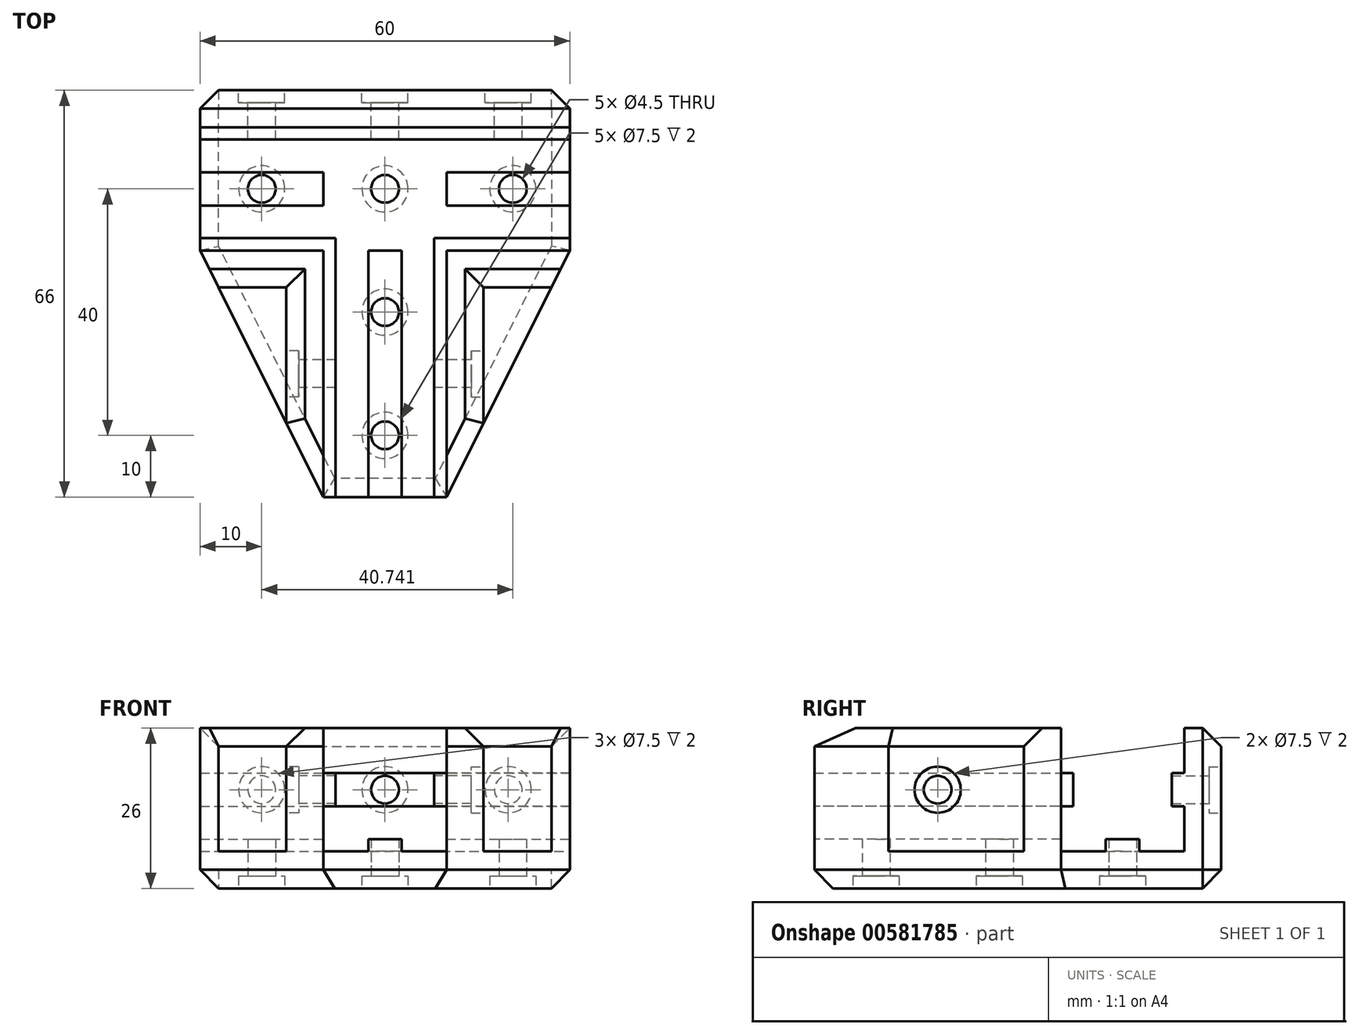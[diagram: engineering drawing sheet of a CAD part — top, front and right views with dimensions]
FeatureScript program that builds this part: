
annotation { "Feature Type Name" : "Feature", "Feature Type Description" : "" }
export const myFeature = defineFeature(function(context is Context, id is Id, definition is map)
    precondition{}
    {
        {
            var Q0;
            Q0=qCreatedBy(makeId("Top.planeOp"),FACE);
            var sketch = newSketch(context, id + "F0", { "sketchPlane" : qUnion([Q0])});
            skLineSegment(sketch, "E0", {"start": v(0, 0) * mm, "end": v(0, 20) * mm, "construction": true});
            skLineSegment(sketch, "E1", {"start": v(0, 0) * mm, "end": v(0, -40) * mm, "construction": true});
            skLineSegment(sketch, "E2", {"start": v(-10, 0) * mm, "end": v(-30, 0) * mm});
            skLineSegment(sketch, "E3", {"start": v(0, 20) * mm, "end": v(-30, 20) * mm});
            skLineSegment(sketch, "E4", {"start": v(-30, 20) * mm, "end": v(-30, 0) * mm});
            skLineSegment(sketch, "E5", {"start": v(0, 20) * mm, "end": v(30, 20) * mm});
            skLineSegment(sketch, "E6", {"start": v(30, 20) * mm, "end": v(30, 0) * mm});
            skLineSegment(sketch, "E7", {"start": v(30, 0) * mm, "end": v(10, 0) * mm});
            skLineSegment(sketch, "E8", {"start": v(0, -40) * mm, "end": v(10, -40) * mm});
            skLineSegment(sketch, "E9", {"start": v(10, -40) * mm, "end": v(10, 0) * mm});
            skLineSegment(sketch, "E10", {"start": v(0, -40) * mm, "end": v(-10, -40) * mm});
            skLineSegment(sketch, "E11", {"start": v(-10, -40) * mm, "end": v(-10, 0) * mm});
            skSolve(sketch);
        }
        {
            var Q0;
            Q0=qSketchRegion(id+"F0",true);
            extrude(context, id + "F1", {"entities" : qUnion([Q0]), "depth" : 6 * mm});
        }
        {
            var Q0;
            Q0=makeQuery(id+"F1.opExtrude","CAP_FACE",FACE,{"disambiguationData":[OSD([sQuery(id+"F0.wireOp",EDGE,"E2"),sQuery(id+"F0.wireOp",EDGE,"E3"),sQuery(id+"F0.wireOp",EDGE,"E4"),sQuery(id+"F0.wireOp",EDGE,"E5"),sQuery(id+"F0.wireOp",EDGE,"E6"),sQuery(id+"F0.wireOp",EDGE,"E7"),sQuery(id+"F0.wireOp",EDGE,"E8"),sQuery(id+"F0.wireOp",EDGE,"E9"),sQuery(id+"F0.wireOp",EDGE,"E10"),sQuery(id+"F0.wireOp",EDGE,"E11")])],"isStart":false});
            var sketch = newSketch(context, id + "F2", { "sketchPlane" : qUnion([Q0])});
            skLineSegment(sketch, "E12", {"start": v(-30, 10) * mm, "end": v(30, 10) * mm, "construction": true});
            skLineSegment(sketch, "E13", {"start": v(0, -40) * mm, "end": v(0, 0) * mm, "construction": true});
            skLineSegment(sketch, "E14", {"start": v(0, 0) * mm, "end": v(-2.71, 0) * mm});
            skLineSegment(sketch, "E15", {"start": v(-2.71, 0) * mm, "end": v(-2.7, -40) * mm});
            skLineSegment(sketch, "E16", {"start": v(2.71, -40) * mm, "end": v(2.71, 0) * mm});
            skLineSegment(sketch, "E17", {"start": v(2.71, 0) * mm, "end": v(0, 0) * mm});
            skLineSegment(sketch, "E18", {"start": v(-2.7, -40) * mm, "end": v(2.71, -40) * mm});
            skLineSegment(sketch, "E19", {"start": v(10, 10) * mm, "end": v(10, 12.7) * mm});
            skLineSegment(sketch, "E20", {"start": v(10, 12.71) * mm, "end": v(30, 12.71) * mm});
            skLineSegment(sketch, "E21", {"start": v(30, 12.71) * mm, "end": v(30, 7.3) * mm});
            skLineSegment(sketch, "E22", {"start": v(30, 7.3) * mm, "end": v(10, 7.29) * mm});
            skLineSegment(sketch, "E23", {"start": v(10, 7.29) * mm, "end": v(10, 10) * mm});
            skLineSegment(sketch, "E24", {"start": v(-30, 12.71) * mm, "end": v(-30, 7.29) * mm});
            skLineSegment(sketch, "E25", {"start": v(-30, 7.29) * mm, "end": v(-10, 7.3) * mm});
            skLineSegment(sketch, "E26", {"start": v(-10, 7.29) * mm, "end": v(-10, 12.71) * mm});
            skLineSegment(sketch, "E27", {"start": v(-10, 12.71) * mm, "end": v(-30, 12.71) * mm});
            skSolve(sketch);
        }
        {
            var Q0;
            Q0=qSketchRegion(id+"F2",true);
            extrude(context, id + "F3", {"entities" : qUnion([Q0]), "operationType" : NewBodyOperationType.ADD, "depth" : 2 * mm});
        }
        {
            var Q0;
            Q0=makeQuery(id+"F1.opExtrude","CAP_FACE",FACE,{"disambiguationData":[OSD([sQuery(id+"F0.wireOp",EDGE,"E2"),sQuery(id+"F0.wireOp",EDGE,"E3"),sQuery(id+"F0.wireOp",EDGE,"E4"),sQuery(id+"F0.wireOp",EDGE,"E5"),sQuery(id+"F0.wireOp",EDGE,"E6"),sQuery(id+"F0.wireOp",EDGE,"E7"),sQuery(id+"F0.wireOp",EDGE,"E8"),sQuery(id+"F0.wireOp",EDGE,"E9"),sQuery(id+"F0.wireOp",EDGE,"E10"),sQuery(id+"F0.wireOp",EDGE,"E11")])],"isStart":true});
            var sketch = newSketch(context, id + "F4", { "sketchPlane" : qUnion([Q0])});
            skCircle(sketch, "E28", {"center": v(-20, -10) * mm, "radius": 2.25 * mm});
            skCircle(sketch, "E29", {"center": v(0, 10) * mm, "radius": 2.25 * mm});
            skCircle(sketch, "E30", {"center": v(0, 30) * mm, "radius": 2.25 * mm});
            skCircle(sketch, "E31", {"center": v(20.74, -10) * mm, "radius": 2.25 * mm});
            skCircle(sketch, "E32", {"center": v(0, -10) * mm, "radius": 2.25 * mm});
            skSolve(sketch);
        }
        {
            var Q0;
            Q0=qSketchRegion(id+"F4",true);
            extrude(context, id + "F5", {"entities" : qUnion([Q0]), "operationType" : NewBodyOperationType.REMOVE, "endBound" : BoundingType.THROUGH_ALL, "oppositeDirection" : true, "depth" : 25 * mm});
        }
        {
            var Q0;
            Q0=makeQuery(id+"F1.opExtrude","CAP_FACE",FACE,{"disambiguationData":[OSD([sQuery(id+"F0.wireOp",EDGE,"E2"),sQuery(id+"F0.wireOp",EDGE,"E3"),sQuery(id+"F0.wireOp",EDGE,"E4"),sQuery(id+"F0.wireOp",EDGE,"E5"),sQuery(id+"F0.wireOp",EDGE,"E6"),sQuery(id+"F0.wireOp",EDGE,"E7"),sQuery(id+"F0.wireOp",EDGE,"E8"),sQuery(id+"F0.wireOp",EDGE,"E9"),sQuery(id+"F0.wireOp",EDGE,"E10"),sQuery(id+"F0.wireOp",EDGE,"E11")])],"isStart":true});
            var sketch = newSketch(context, id + "F6", { "sketchPlane" : qUnion([Q0])});
            skCircle(sketch, "E33", {"center": v(0, 30) * mm, "radius": 3.75 * mm});
            skCircle(sketch, "E34", {"center": v(0, 10) * mm, "radius": 3.75 * mm});
            skCircle(sketch, "E35", {"center": v(20.74, -10) * mm, "radius": 3.75 * mm});
            skCircle(sketch, "E36", {"center": v(-20, -10) * mm, "radius": 3.75 * mm});
            skCircle(sketch, "E37", {"center": v(0, -10) * mm, "radius": 3.75 * mm});
            skSolve(sketch);
        }
        {
            var Q0;
            Q0=qSketchRegion(id+"F6",true);
            extrude(context, id + "F7", {"entities" : qUnion([Q0]), "operationType" : NewBodyOperationType.REMOVE, "oppositeDirection" : true, "depth" : 2 * mm});
        }
        {
            var Q0;
            Q0=makeQuery(id+"F1.opExtrude","CAP_FACE",FACE,{"disambiguationData":[OSD([sQuery(id+"F0.wireOp",EDGE,"E2"),sQuery(id+"F0.wireOp",EDGE,"E3"),sQuery(id+"F0.wireOp",EDGE,"E4"),sQuery(id+"F0.wireOp",EDGE,"E5"),sQuery(id+"F0.wireOp",EDGE,"E6"),sQuery(id+"F0.wireOp",EDGE,"E7"),sQuery(id+"F0.wireOp",EDGE,"E8"),sQuery(id+"F0.wireOp",EDGE,"E9"),sQuery(id+"F0.wireOp",EDGE,"E10"),sQuery(id+"F0.wireOp",EDGE,"E11")])],"isStart":true});
            var sketch = newSketch(context, id + "F8", { "sketchPlane" : qUnion([Q0])});
            skLineSegment(sketch, "E38", {"start": v(-10, 40) * mm, "end": v(-30, 0) * mm});
            skLineSegment(sketch, "E39", {"start": v(-30, 0) * mm, "end": v(-10, 0) * mm});
            skLineSegment(sketch, "E40", {"start": v(-10, 0) * mm, "end": v(-10, 40) * mm});
            skLineSegment(sketch, "E41", {"start": v(10, 40) * mm, "end": v(10, 0) * mm});
            skLineSegment(sketch, "E42", {"start": v(10, 0) * mm, "end": v(30, 0) * mm});
            skLineSegment(sketch, "E43", {"start": v(30, 0) * mm, "end": v(10, 40) * mm});
            skLineSegment(sketch, "E44", {"start": v(-30, -20) * mm, "end": v(-30, -26) * mm});
            skLineSegment(sketch, "E45", {"start": v(-30, -26) * mm, "end": v(30, -26) * mm});
            skLineSegment(sketch, "E46", {"start": v(30, -26) * mm, "end": v(30, -20) * mm});
            skLineSegment(sketch, "E47", {"start": v(30, -20) * mm, "end": v(-30, -20) * mm});
            skSolve(sketch);
        }
        {
            var Q0;
            Q0=qSketchRegion(id+"F8",true);
            extrude(context, id + "F9", {"entities" : qUnion([Q0]), "operationType" : NewBodyOperationType.ADD, "oppositeDirection" : true, "depth" : 6 * mm});
        }
        {
            var Q0;
            Q0=makeQuery(id+"F9.boolean.opBoolean","MERGE",FACE,{"derivedFrom":[makeQuery(id+"F1.opExtrude","CAP_FACE",FACE,{"disambiguationData":[OSD([sQuery(id+"F0.wireOp",EDGE,"E2"),sQuery(id+"F0.wireOp",EDGE,"E3"),sQuery(id+"F0.wireOp",EDGE,"E4"),sQuery(id+"F0.wireOp",EDGE,"E5"),sQuery(id+"F0.wireOp",EDGE,"E6"),sQuery(id+"F0.wireOp",EDGE,"E7"),sQuery(id+"F0.wireOp",EDGE,"E8"),sQuery(id+"F0.wireOp",EDGE,"E9"),sQuery(id+"F0.wireOp",EDGE,"E10"),sQuery(id+"F0.wireOp",EDGE,"E11")])],"isStart":false}),makeQuery(id+"F9.opExtrude","CAP_FACE",FACE,{"disambiguationData":[OSD([sQuery(id+"F8.wireOp",EDGE,"E38"),sQuery(id+"F8.wireOp",EDGE,"E39"),sQuery(id+"F8.wireOp",EDGE,"E40")])],"isStart":false}),makeQuery(id+"F9.opExtrude","CAP_FACE",FACE,{"disambiguationData":[OSD([sQuery(id+"F8.wireOp",EDGE,"E41"),sQuery(id+"F8.wireOp",EDGE,"E42"),sQuery(id+"F8.wireOp",EDGE,"E43")])],"isStart":false})]});
            var sketch = newSketch(context, id + "F10", { "sketchPlane" : qUnion([Q0])});
            skLineSegment(sketch, "E48", {"start": v(0, 0) * mm, "end": v(10, 0) * mm, "construction": true});
            skPoint(sketch, "E48.endSnap0", {"position": v(0, 0) * mm});
            skLineSegment(sketch, "E49", {"start": v(0, 0) * mm, "end": v(-10, 0) * mm, "construction": true});
            skLineSegment(sketch, "E50", {"start": v(10, 0) * mm, "end": v(10, -40) * mm});
            skLineSegment(sketch, "E51", {"start": v(10, 0) * mm, "end": v(30, 0) * mm});
            skLineSegment(sketch, "E52", {"start": v(20, 0) * mm, "end": v(20, -6) * mm, "construction": true});
            skLineSegment(sketch, "E53", {"start": v(10, -20) * mm, "end": v(16, -20) * mm, "construction": true});
            skLineSegment(sketch, "E54", {"start": v(27, -6) * mm, "end": v(16, -6) * mm});
            skLineSegment(sketch, "E55", {"start": v(16, -6) * mm, "end": v(16, -28) * mm});
            skLineSegment(sketch, "E56", {"start": v(16, -28) * mm, "end": v(10, -40) * mm});
            skLineSegment(sketch, "E57", {"start": v(27, -6) * mm, "end": v(30, 0) * mm});
            skLineSegment(sketch, "E58", {"start": v(-10, 0) * mm, "end": v(-10, -40) * mm});
            skLineSegment(sketch, "E59", {"start": v(-30, 0) * mm, "end": v(-10, 0) * mm});
            skLineSegment(sketch, "E60", {"start": v(-20, 0) * mm, "end": v(-20, -6) * mm, "construction": true});
            skLineSegment(sketch, "E61", {"start": v(-10, -20) * mm, "end": v(-16, -20) * mm, "construction": true});
            skLineSegment(sketch, "E62", {"start": v(-27, -6) * mm, "end": v(-16, -6) * mm});
            skLineSegment(sketch, "E63", {"start": v(-16, -6) * mm, "end": v(-16, -28) * mm});
            skLineSegment(sketch, "E64", {"start": v(-16, -28) * mm, "end": v(-10, -40) * mm});
            skLineSegment(sketch, "E65", {"start": v(-27, -6) * mm, "end": v(-30, 0) * mm});
            skLineSegment(sketch, "E66.bottom", {"start": v(-30, 26) * mm, "end": v(30, 26) * mm});
            skLineSegment(sketch, "E66.top", {"start": v(-30, 20) * mm, "end": v(30, 20) * mm});
            skLineSegment(sketch, "E66.left", {"start": v(-30, 26) * mm, "end": v(-30, 20) * mm});
            skLineSegment(sketch, "E66.right", {"start": v(30, 26) * mm, "end": v(30, 20) * mm});
            skSolve(sketch);
        }
        {
            var Q0;
            Q0=qSketchRegion(id+"F10",true);
            extrude(context, id + "F11", {"entities" : qUnion([Q0]), "operationType" : NewBodyOperationType.ADD, "depth" : 20 * mm});
        }
        {
            var Q0;
            Q0=makeQuery(id+"F11.boolean.opBoolean","MERGE",FACE,{"derivedFrom":[makeQuery(id+"F9.boolean.opBoolean","MERGE",FACE,{"derivedFrom":[makeQuery(id+"F3.boolean.opBoolean","MERGE",FACE,{"derivedFrom":[makeQuery(id+"F1.opExtrude","SWEPT_FACE",FACE,{"disambiguationData":[OSD([sQuery(id+"F0.wireOp",EDGE,"E6")])]}),makeQuery(id+"F3.opExtrude","SWEPT_FACE",FACE,{"disambiguationData":[OSD([sQuery(id+"F2.wireOp",EDGE,"E21")])]})]}),makeQuery(id+"F9.opExtrude","SWEPT_FACE",FACE,{"disambiguationData":[OSD([sQuery(id+"F8.wireOp",EDGE,"E46")])]})]}),makeQuery(id+"F11.opExtrude","SWEPT_FACE",FACE,{"disambiguationData":[OSD([sQuery(id+"F10.wireOp",EDGE,"E66.right")])]})]});
            var sketch = newSketch(context, id + "F12", { "sketchPlane" : qUnion([Q0])});
            skLineSegment(sketch, "E67", {"start": v(20, 16) * mm, "end": v(20, 13.29) * mm});
            skLineSegment(sketch, "E68", {"start": v(20, 13.29) * mm, "end": v(18, 13.29) * mm});
            skLineSegment(sketch, "E69", {"start": v(18, 13.29) * mm, "end": v(18, 18.71) * mm});
            skLineSegment(sketch, "E70", {"start": v(18, 18.71) * mm, "end": v(20, 18.71) * mm});
            skLineSegment(sketch, "E71", {"start": v(20, 18.71) * mm, "end": v(20, 16) * mm});
            skSolve(sketch);
        }
        {
            var Q0;
            Q0=qSketchRegion(id+"F12",true);
            extrude(context, id + "F13", {"entities" : qUnion([Q0]), "operationType" : NewBodyOperationType.ADD, "oppositeDirection" : true, "depth" : 60 * mm});
        }
        {
            var Q0;
            Q0=makeQuery(id+"F11.opExtrude","SWEPT_FACE",FACE,{"disambiguationData":[OSD([sQuery(id+"F10.wireOp",EDGE,"E58")])]});
            var sketch = newSketch(context, id + "F14", { "sketchPlane" : qUnion([Q0])});
            skLineSegment(sketch, "E72", {"start": v(0, 16) * mm, "end": v(0, 18.71) * mm});
            skLineSegment(sketch, "E73", {"start": v(0, 18.71) * mm, "end": v(2, 18.71) * mm});
            skLineSegment(sketch, "E74", {"start": v(2, 18.71) * mm, "end": v(2, 13.29) * mm});
            skLineSegment(sketch, "E75", {"start": v(2, 13.29) * mm, "end": v(0, 13.29) * mm});
            skLineSegment(sketch, "E76", {"start": v(0, 13.29) * mm, "end": v(0, 16) * mm});
            skSolve(sketch);
        }
        {
            var Q0;
            Q0=qSketchRegion(id+"F14",true);
            extrude(context, id + "F15", {"entities" : qUnion([Q0]), "operationType" : NewBodyOperationType.ADD, "oppositeDirection" : true, "depth" : 20 * mm});
        }
        {
            var Q0;
            Q0=makeQuery(id+"F15.boolean.opBoolean","MERGE",FACE,{"derivedFrom":[makeQuery(id+"F11.opExtrude","SWEPT_FACE",FACE,{"disambiguationData":[OSD([sQuery(id+"F10.wireOp",EDGE,"E58")])]}),makeQuery(id+"F15.opExtrude","CAP_FACE",FACE,{"disambiguationData":[OSD([sQuery(id+"F14.wireOp",EDGE,"E72"),sQuery(id+"F14.wireOp",EDGE,"E73"),sQuery(id+"F14.wireOp",EDGE,"E74"),sQuery(id+"F14.wireOp",EDGE,"E75"),sQuery(id+"F14.wireOp",EDGE,"E76")])],"isStart":true})]});
            var sketch = newSketch(context, id + "F16", { "sketchPlane" : qUnion([Q0])});
            skLineSegment(sketch, "E77.bottom", {"start": v(2, 18.71) * mm, "end": v(-40, 18.71) * mm});
            skLineSegment(sketch, "E77.top", {"start": v(2, 13.29) * mm, "end": v(-40, 13.29) * mm});
            skLineSegment(sketch, "E77.left", {"start": v(2, 18.71) * mm, "end": v(2, 13.29) * mm});
            skLineSegment(sketch, "E77.right", {"start": v(-40, 18.71) * mm, "end": v(-40, 13.29) * mm});
            skSolve(sketch);
        }
        {
            var Q0;
            Q0=qSketchRegion(id+"F16",true);
            extrude(context, id + "F17", {"entities" : qUnion([Q0]), "operationType" : NewBodyOperationType.ADD, "depth" : 2 * mm});
        }
        {
            var Q0;
            Q0=makeQuery(id+"F11.opExtrude","SWEPT_FACE",FACE,{"disambiguationData":[OSD([sQuery(id+"F10.wireOp",EDGE,"E50")])]});
            var sketch = newSketch(context, id + "F18", { "sketchPlane" : qUnion([Q0])});
            skLineSegment(sketch, "E78", {"start": v(0, 16) * mm, "end": v(0, 18.71) * mm});
            skLineSegment(sketch, "E79", {"start": v(0, 18.71) * mm, "end": v(-2, 18.71) * mm});
            skLineSegment(sketch, "E80", {"start": v(-2, 18.71) * mm, "end": v(-2, 13.29) * mm});
            skLineSegment(sketch, "E81", {"start": v(-2, 13.29) * mm, "end": v(0, 13.29) * mm});
            skLineSegment(sketch, "E82", {"start": v(0, 13.29) * mm, "end": v(0, 16) * mm});
            skSolve(sketch);
        }
        {
            var Q0;
            Q0=qSketchRegion(id+"F18",true);
            extrude(context, id + "F19", {"entities" : qUnion([Q0]), "operationType" : NewBodyOperationType.ADD, "oppositeDirection" : true, "depth" : 20 * mm});
        }
        {
            var Q0;
            Q0=makeQuery(id+"F19.boolean.opBoolean","MERGE",FACE,{"derivedFrom":[makeQuery(id+"F11.opExtrude","SWEPT_FACE",FACE,{"disambiguationData":[OSD([sQuery(id+"F10.wireOp",EDGE,"E50")])]}),makeQuery(id+"F19.opExtrude","CAP_FACE",FACE,{"disambiguationData":[OSD([sQuery(id+"F18.wireOp",EDGE,"E78"),sQuery(id+"F18.wireOp",EDGE,"E79"),sQuery(id+"F18.wireOp",EDGE,"E80"),sQuery(id+"F18.wireOp",EDGE,"E81"),sQuery(id+"F18.wireOp",EDGE,"E82")])],"isStart":true})]});
            var sketch = newSketch(context, id + "F20", { "sketchPlane" : qUnion([Q0])});
            skLineSegment(sketch, "E83.bottom", {"start": v(-2, 13.29) * mm, "end": v(40, 13.29) * mm});
            skLineSegment(sketch, "E83.top", {"start": v(-2, 18.71) * mm, "end": v(40, 18.71) * mm});
            skLineSegment(sketch, "E83.left", {"start": v(-2, 13.29) * mm, "end": v(-2, 18.71) * mm});
            skLineSegment(sketch, "E83.right", {"start": v(40, 13.29) * mm, "end": v(40, 18.71) * mm});
            skSolve(sketch);
        }
        {
            var Q0;
            Q0=qSketchRegion(id+"F20",true);
            extrude(context, id + "F21", {"entities" : qUnion([Q0]), "operationType" : NewBodyOperationType.ADD, "depth" : 2 * mm});
        }
        {
            var Q0;
            Q0=makeQuery(id+"F11.opExtrude","SWEPT_FACE",FACE,{"disambiguationData":[OSD([sQuery(id+"F10.wireOp",EDGE,"E63")])]});
            var sketch = newSketch(context, id + "F22", { "sketchPlane" : qUnion([Q0])});
            skCircle(sketch, "E84", {"center": v(20, 16) * mm, "radius": 2.25 * mm});
            skSolve(sketch);
        }
        {
            var Q0;
            Q0=qSketchRegion(id+"F22",true);
            extrude(context, id + "F23", {"entities" : qUnion([Q0]), "operationType" : NewBodyOperationType.REMOVE, "endBound" : BoundingType.THROUGH_ALL, "oppositeDirection" : true, "depth" : 25 * mm});
        }
        {
            var Q0;
            Q0=makeQuery(id+"F11.boolean.opBoolean","MERGE",FACE,{"derivedFrom":[makeQuery(id+"F9.opExtrude","SWEPT_FACE",FACE,{"disambiguationData":[OSD([sQuery(id+"F8.wireOp",EDGE,"E45")])]}),makeQuery(id+"F11.opExtrude","SWEPT_FACE",FACE,{"disambiguationData":[OSD([sQuery(id+"F10.wireOp",EDGE,"E66.bottom")])]})]});
            var sketch = newSketch(context, id + "F24", { "sketchPlane" : qUnion([Q0])});
            skCircle(sketch, "E85", {"center": v(-20, 16) * mm, "radius": 2.25 * mm});
            skCircle(sketch, "E86", {"center": v(0, 16) * mm, "radius": 2.25 * mm});
            skCircle(sketch, "E87", {"center": v(20, 16) * mm, "radius": 2.25 * mm});
            skSolve(sketch);
        }
        {
            var Q0;
            Q0=qSketchRegion(id+"F24",true);
            extrude(context, id + "F25", {"entities" : qUnion([Q0]), "operationType" : NewBodyOperationType.REMOVE, "endBound" : BoundingType.UP_TO_NEXT, "oppositeDirection" : true, "depth" : 8 * mm});
        }
        {
            var Q0;
            Q0=makeQuery(id+"F11.opExtrude","SWEPT_FACE",FACE,{"disambiguationData":[OSD([sQuery(id+"F10.wireOp",EDGE,"E55")])]});
            var sketch = newSketch(context, id + "F26", { "sketchPlane" : qUnion([Q0])});
            skCircle(sketch, "E88", {"center": v(-20, 16) * mm, "radius": 3.75 * mm});
            skSolve(sketch);
        }
        {
            var Q0;
            Q0=qSketchRegion(id+"F26",true);
            extrude(context, id + "F27", {"entities" : qUnion([Q0]), "operationType" : NewBodyOperationType.REMOVE, "oppositeDirection" : true, "depth" : 2 * mm});
        }
        {
            var Q0;
            Q0=makeQuery(id+"F11.opExtrude","SWEPT_FACE",FACE,{"disambiguationData":[OSD([sQuery(id+"F10.wireOp",EDGE,"E63")])]});
            var sketch = newSketch(context, id + "F28", { "sketchPlane" : qUnion([Q0])});
            skCircle(sketch, "E89", {"center": v(20, 16) * mm, "radius": 3.75 * mm});
            skSolve(sketch);
        }
        {
            var Q0;
            Q0=qSketchRegion(id+"F28",true);
            extrude(context, id + "F29", {"entities" : qUnion([Q0]), "operationType" : NewBodyOperationType.REMOVE, "oppositeDirection" : true, "depth" : 2 * mm});
        }
        {
            var Q0;
            Q0=makeQuery(id+"F11.boolean.opBoolean","MERGE",FACE,{"derivedFrom":[makeQuery(id+"F9.opExtrude","SWEPT_FACE",FACE,{"disambiguationData":[OSD([sQuery(id+"F8.wireOp",EDGE,"E45")])]}),makeQuery(id+"F11.opExtrude","SWEPT_FACE",FACE,{"disambiguationData":[OSD([sQuery(id+"F10.wireOp",EDGE,"E66.bottom")])]})]});
            var sketch = newSketch(context, id + "F30", { "sketchPlane" : qUnion([Q0])});
            skCircle(sketch, "E90", {"center": v(-20, 16) * mm, "radius": 3.75 * mm});
            skCircle(sketch, "E91", {"center": v(0, 16) * mm, "radius": 3.75 * mm});
            skCircle(sketch, "E92", {"center": v(20, 16) * mm, "radius": 3.75 * mm});
            skSolve(sketch);
        }
        {
            var Q0;
            Q0=qSketchRegion(id+"F30",true);
            extrude(context, id + "F31", {"entities" : qUnion([Q0]), "operationType" : NewBodyOperationType.REMOVE, "oppositeDirection" : true, "depth" : 2 * mm});
        }
        {
            var Q0;
            Q0=makeQuery(id+"F9.opExtrude","CAP_EDGE",EDGE,{"disambiguationData":[OSD([sQuery(id+"F8.wireOp",EDGE,"E45")])],"isStart":true});
            var Q1;
            Q1=makeQuery(id+"F11.boolean.opBoolean","MERGE",EDGE,{"derivedFrom":[makeQuery(id+"F9.opExtrude","SWEPT_EDGE",EDGE,{"disambiguationData":[OSD([sQuery(id+"F8.wireOp",EDGE,"E45"),sQuery(id+"F8.wireOp",EDGE,"E46")])]}),makeQuery(id+"F11.opExtrude","SWEPT_EDGE",EDGE,{"disambiguationData":[OSD([sQuery(id+"F10.wireOp",EDGE,"E66.bottom"),sQuery(id+"F10.wireOp",EDGE,"E66.right")])]})]});
            var Q2;
            Q2=makeQuery(id+"F11.boolean.opBoolean","MERGE",EDGE,{"derivedFrom":[makeQuery(id+"F9.opExtrude","SWEPT_EDGE",EDGE,{"disambiguationData":[OSD([sQuery(id+"F8.wireOp",EDGE,"E44"),sQuery(id+"F8.wireOp",EDGE,"E45")])]}),makeQuery(id+"F11.opExtrude","SWEPT_EDGE",EDGE,{"disambiguationData":[OSD([sQuery(id+"F10.wireOp",EDGE,"E66.bottom"),sQuery(id+"F10.wireOp",EDGE,"E66.left")])]})]});
            var Q3;
            Q3=makeQuery(id+"F9.boolean.opBoolean","MERGE",EDGE,{"derivedFrom":[makeQuery(id+"F1.opExtrude","CAP_EDGE",EDGE,{"disambiguationData":[OSD([sQuery(id+"F0.wireOp",EDGE,"E4")])],"isStart":true}),makeQuery(id+"F9.opExtrude","CAP_EDGE",EDGE,{"disambiguationData":[OSD([sQuery(id+"F8.wireOp",EDGE,"E44")])],"isStart":true})]});
            var Q4;
            Q4=makeQuery(id+"F9.boolean.opBoolean","MERGE",EDGE,{"derivedFrom":[makeQuery(id+"F1.opExtrude","CAP_EDGE",EDGE,{"disambiguationData":[OSD([sQuery(id+"F0.wireOp",EDGE,"E6")])],"isStart":true}),makeQuery(id+"F9.opExtrude","CAP_EDGE",EDGE,{"disambiguationData":[OSD([sQuery(id+"F8.wireOp",EDGE,"E46")])],"isStart":true})]});
            var Q5;
            Q5=makeQuery(id+"F9.opExtrude","CAP_EDGE",EDGE,{"disambiguationData":[OSD([sQuery(id+"F8.wireOp",EDGE,"E43")])],"isStart":true});
            var Q6;
            Q6=makeQuery(id+"F9.opExtrude","CAP_EDGE",EDGE,{"disambiguationData":[OSD([sQuery(id+"F8.wireOp",EDGE,"E38")])],"isStart":true});
            var Q7;
            Q7=makeQuery(id+"F1.opExtrude","CAP_EDGE",EDGE,{"disambiguationData":[OSD([sQuery(id+"F0.wireOp",EDGE,"E8"),sQuery(id+"F0.wireOp",EDGE,"E10")])],"isStart":true});
            var Q8;
            Q8=makeQuery(id+"F11.opExtrude","CAP_EDGE",EDGE,{"disambiguationData":[OSD([sQuery(id+"F10.wireOp",EDGE,"E66.bottom")])],"isStart":false});
            var Q9;
            Q9=makeQuery(id+"F11.opExtrude","CAP_EDGE",EDGE,{"disambiguationData":[OSD([sQuery(id+"F10.wireOp",EDGE,"E62")])],"isStart":false});
            var Q10;
            Q10=makeQuery(id+"F11.opExtrude","CAP_EDGE",EDGE,{"disambiguationData":[OSD([sQuery(id+"F10.wireOp",EDGE,"E63")])],"isStart":false});
            var Q11;
            Q11=makeQuery(id+"F11.opExtrude","CAP_EDGE",EDGE,{"disambiguationData":[OSD([sQuery(id+"F10.wireOp",EDGE,"E55")])],"isStart":false});
            var Q12;
            Q12=makeQuery(id+"F11.opExtrude","CAP_EDGE",EDGE,{"disambiguationData":[OSD([sQuery(id+"F10.wireOp",EDGE,"E54")])],"isStart":false});
            var Q13;
            Q13=makeQuery(id+"F11.opExtrude","CAP_EDGE",EDGE,{"disambiguationData":[OSD([sQuery(id+"F10.wireOp",EDGE,"E64")])],"isStart":false});
            var Q14;
            Q14=makeQuery(id+"F11.opExtrude","CAP_EDGE",EDGE,{"disambiguationData":[OSD([sQuery(id+"F10.wireOp",EDGE,"E56")])],"isStart":false});
            chamfer(context, id + "F32", {"entities" : qUnion([Q0, Q1, Q2, Q3, Q4, Q5, Q6, Q7, Q8, Q9, Q10, Q11, Q12, Q13, Q14]), "width" : 3 * mm, "tangentPropagation" : true});
        }
    });
